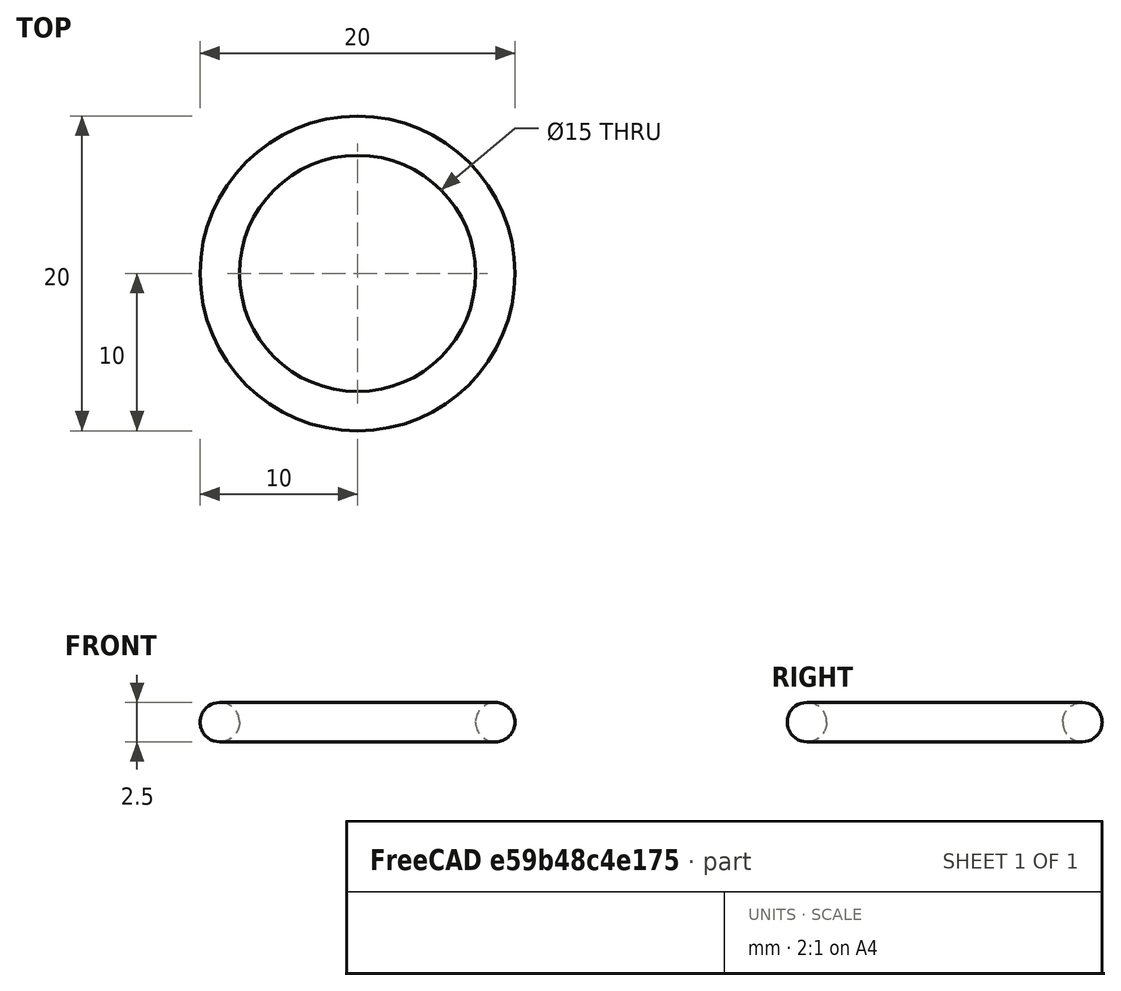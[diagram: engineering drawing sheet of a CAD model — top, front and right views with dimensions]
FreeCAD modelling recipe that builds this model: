
FCSTD DOCUMENT  (FreeCAD 0.18R4 (GitTag))
Label: RubberGaskey_20mm
License: All rights reserved
LicenseURL: http://en.wikipedia.org/wiki/All_rights_reserved
objects: Sketcher::SketchObject×1, PartDesign::Pad×1, PartDesign::Fillet×1, PartDesign::Body×1
note: 5 computed .brp shape members not serialized (recipe doc carries the construction recipe); baked Part::Feature solids carry a one-line shape summary decoded from their .brp

FEATURE [Sketcher::SketchObject] Sketch
  MapMode = 5
  Support = -> [XY_Plane]
  sketch-geometry (2):
    g0: Circle CenterX=0 CenterY=0 CenterZ=0 NormalX=0 NormalY=0 NormalZ=1 AngleXU=0 Radius=7.5
    g1: Circle CenterX=0 CenterY=0 CenterZ=0 NormalX=0 NormalY=0 NormalZ=1 AngleXU=0 Radius=10
  constraints (4):
    c: Coincident(g0,g-1)
    c: Coincident(g1,g0)
    c: Diameter(g1) = 20
    c: Diameter(g0) = 15
FEATURE [PartDesign::Pad] Pad
  Length = 2.5
  Length2 = 100
  Profile = -> Sketch
  Type = 0
FEATURE [PartDesign::Fillet] Fillet
  Base = -> Pad [Edge6,Edge5,Edge3,Edge2]
  BaseFeature = -> Pad
  Radius = 1.249
FEATURE [PartDesign::Body] Body  label="RubberGasket_20mm"
  Group = -> [Sketch,Pad,Fillet]
  Origin = -> Origin
  Tip = -> Fillet
